# Revit family: Haworth_BuzziBlinds_ClassicScreen_StraightBase
name_source: partatom
category: Furniture
revit_build: Autodesk Revit 2018 (Build: 20170223_1515(x64)
units: mm (PartAtom-declared; Revit-internal decimal feet)

## family parameters
Always vertical = Yes
Cut with Voids When Loaded = No
OmniClass Number = 23.40.20.00
OmniClass Title = General Furniture and Specialties
Room Calculation Point = No
Shared = No
Work Plane-Based = No

## types (6) — shared parameters
Actual Depth = 14.75 "
Actual Width = 39.37 "
Assembly Code = E2020200
Manufacturer = Haworth
Model = HCBZ-BD
Revision = 1
Screen Spacing = 7.874 "
Size = Verify Final Dim. w/ Haworth
URL = http://www.haworth.com
URL - Product = https://www.haworth.com
Warranty = http://www.haworth.com

## per-type parameters (varying)
| type | Actual Height | Casters | Description | Large | Medium | Small |
| HCBZ-BDC1-R - Small Screen - Without Casters | 45.28 " | No | Haworth BuzziBlinds - Small Classic Screen - Without Casters | No | No | Yes |
| HCBZ-BDC1-RC - Small Screen - With Casters | 45.28 " | Yes | Haworth BuzziBlinds - Small Classic Screen - With Casters | No | No | Yes |
| HCBZ-BDC2-RC - Medium Screen - With Casters | 59.06 " | Yes | Haworth BuzziBlinds - Medium Classic Screen - With Casters | No | Yes | No |
| HCBZ-BDC2-R - Medium Screen - Without Casters | 59.06 " | No | Haworth BuzziBlinds - Medium Classic Screen - Without Casters | No | Yes | No |
| HCBZ-BDC3-RC - Large Screen - With Casters | 72.83 " | Yes | Haworth BuzziBlinds - Large Classic Screen - With Casters | Yes | No | No |
| HCBZ-BDC3-R - Large Screen - Without Casters | 72.83 " | No | Haworth BuzziBlinds - Large Classic Screen - Without Casters | Yes | No | No |

## geometry (parser evidence)
native form markers: Sweep x6
no freeform markers — native parametric forms only
